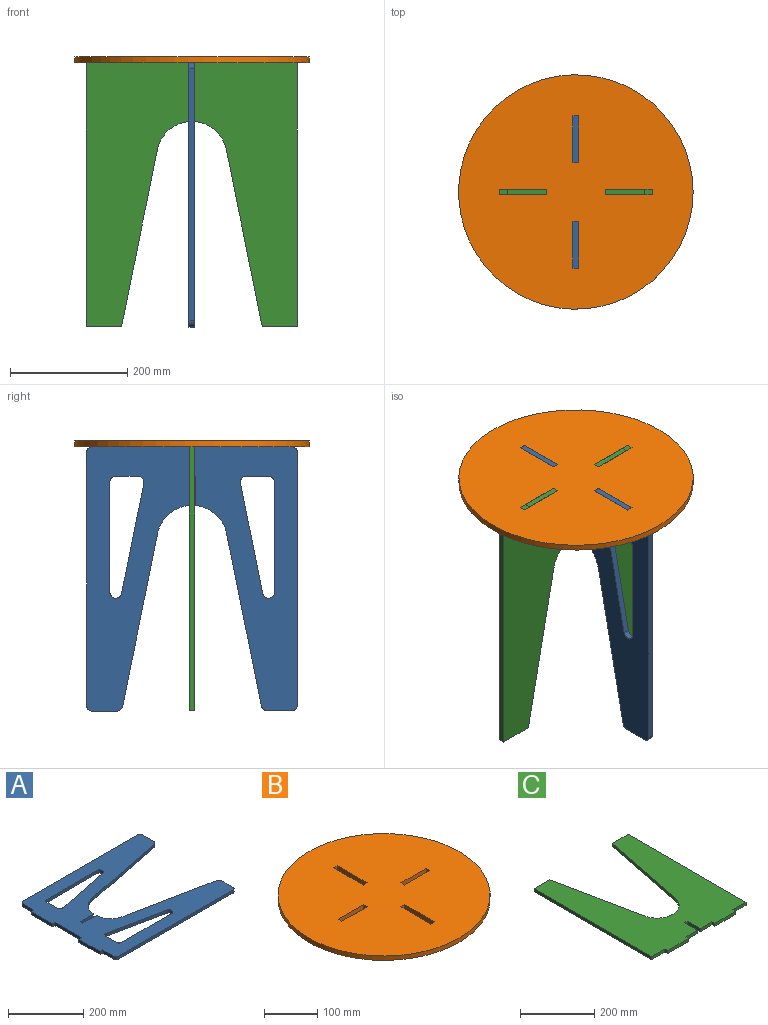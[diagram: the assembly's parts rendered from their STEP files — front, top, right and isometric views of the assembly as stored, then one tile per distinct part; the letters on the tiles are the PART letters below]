
ASSEMBLY  parts=3 mates=2
PART A: 40 faces, bbox 460.6x360x10 mm
  f0: cylinder r=10mm len=10mm, axis (0,0,-1), area 157.1mm2, adj f1,f37,f38,f39
  f1: plane 41.82x10mm, normal (1,0,0), area 418.2mm2, adj f0,f2,f38,f39
  f2: cylinder r=10mm len=10mm, axis (0,0,-1), area 137.2mm2, adj f1,f3,f38,f39
  f3: plane 294.28x59.41mm, normal (0.2,0.98,0), area 3002.1mm2, adj f2,f4,f38,f39
  f4: cylinder r=60mm len=53.81mm, axis (0,0,-1), area 772.9mm2, adj f3,f5,f38,f39
  f5: plane 49.99x10mm, normal (0,1,0), area 499.9mm2, adj f4,f6,f38,f39
  f6: plane 10x10mm, normal (1,0,0), area 100mm2, adj f5,f7,f38,f39
  f7: plane 50x10mm, normal (0,-1,0), area 500mm2, adj f6,f8,f38,f39
  f8: cylinder r=60mm len=53.81mm, axis (0,0,-1), area 772.6mm2, adj f7,f9,f38,f39
  f9: plane 294.95x59.73mm, normal (0.2,-0.98,0), area 3009.3mm2, adj f8,f10,f38,f39
  f10: cylinder r=10mm len=10mm, axis (0,0,-1), area 137.1mm2, adj f9,f11,f38,f39
  f11: plane 41.82x10mm, normal (1,0,0), area 418.2mm2, adj f10,f12,f38,f39
  f12: cylinder r=10mm len=10mm, axis (0,0,-1), area 157.1mm2, adj f11,f13,f38,f39
  f13: plane 430.63x10mm, normal (0,1,0), area 4306.3mm2, adj f12,f14,f38,f39
  f14: cylinder r=10mm len=10mm, axis (0,0,-1), area 157.1mm2, adj f13,f15,f38,f39
  f15: plane 40x10mm, normal (-1,0,0), area 400mm2, adj f14,f16,f38,f39
  f16: plane 10x10mm, normal (0,1,0), area 100mm2, adj f15,f17,f38,f39
  f17: plane 80x10mm, normal (-1,0,0), area 800mm2, adj f16,f18,f38,f39
  f18: plane 10x10mm, normal (0,-1,0), area 100mm2, adj f17,f19,f38,f39
  f19: plane 100x10mm, normal (-1,0,0), area 1000mm2, adj f18,f20,f38,f39
  f20: plane 10x10mm, normal (0,1,0), area 100mm2, adj f19,f21,f38,f39
  f21: plane 80x10mm, normal (-1,0,0), area 800mm2, adj f20,f22,f38,f39
  f22: plane 10x10mm, normal (0,-1,0), area 100mm2, adj f21,f23,f38,f39
  f23: plane 40x10mm, normal (-1,0,0), area 400mm2, adj f22,f24,f38,f39
  f24: cylinder r=10mm len=10mm, axis (0,0,-1), area 157.1mm2, adj f23,f37,f38,f39
  f25: cylinder r=10mm len=11.98mm, axis (0,0,-1), area 177.1mm2, adj f26,f35,f38,f39
  f26: plane 38.09x10mm, normal (1,0,0), area 380.9mm2, adj f25,f27,f38,f39
  f27: cylinder r=10mm len=10mm, axis (0,0,-1), area 157.1mm2, adj f26,f28,f38,f39
  f28: plane 188.09x10mm, normal (0,-1,0), area 1880.9mm2, adj f27,f29,f38,f39
  f29: cylinder r=10mm len=19.8mm, axis (0,0,-1), area 294.2mm2, adj f28,f35,f38,f39
  f30: plane 188.09x10mm, normal (0,1,0), area 1880.9mm2, adj f31,f36,f38,f39
  f31: cylinder r=10mm len=10mm, axis (0,0,-1), area 157.1mm2, adj f30,f32,f38,f39
  f32: plane 38.09x10mm, normal (1,0,0), area 380.9mm2, adj f31,f33,f38,f39
  f33: cylinder r=10mm len=11.98mm, axis (0,0,-1), area 177.1mm2, adj f32,f34,f38,f39
  f34: plane 188.09x38.09mm, normal (-0.2,-0.98,0), area 1919.1mm2, adj f33,f36,f38,f39
  f35: plane 188.09x38.09mm, normal (-0.2,0.98,0), area 1919.1mm2, adj f25,f29,f38,f39
  f36: cylinder r=10mm len=19.8mm, axis (0,0,-1), area 294.2mm2, adj f30,f34,f38,f39
  f37: plane 430x10mm, normal (0,-1,0), area 4300mm2, adj f0,f24,f38,f39
  f38: plane 460.63x360mm, normal (0,0,1), area 88597.3mm2, adj f0,f1,f2,f3,f4,f5,f6,f7
  f39: plane 460.63x360mm, normal (0,0,-1), area 88597.3mm2, adj f0,f1,f2,f3,f4,f5,f6,f7
PART B: 19 faces, bbox 400x400x10 mm
  f0: plane 10x10mm, normal (-1,0,0), area 100mm2, adj f1,f12,f17,f18
  f1: plane 67.44x10mm, normal (0,1,0), area 674.4mm2, adj f0,f2,f17,f18
  f2: plane 10x10mm, normal (1,0,0), area 100mm2, adj f1,f12,f17,f18
  f3: plane 10x10mm, normal (0,1,0), area 100mm2, adj f4,f13,f17,f18
  f4: plane 80x10mm, normal (1,0,0), area 800mm2, adj f3,f5,f17,f18
  f5: plane 10x10mm, normal (0,-1,0), area 100mm2, adj f4,f13,f17,f18
  f6: plane 10x10mm, normal (0,1,0), area 100mm2, adj f7,f14,f17,f18
  f7: plane 80x10mm, normal (1,0,0), area 800mm2, adj f6,f8,f17,f18
  f8: plane 10x10mm, normal (0,-1,0), area 100mm2, adj f7,f14,f17,f18
  f9: plane 67.44x10mm, normal (0,1,0), area 674.4mm2, adj f10,f15,f17,f18
  f10: plane 10x10mm, normal (1,0,0), area 100mm2, adj f9,f11,f17,f18
  f11: plane 67.44x10mm, normal (0,-1,0), area 674.4mm2, adj f10,f15,f17,f18
  f12: plane 67.44x10mm, normal (0,-1,0), area 674.4mm2, adj f0,f2,f17,f18
  f13: plane 80x10mm, normal (-1,0,0), area 800mm2, adj f3,f5,f17,f18
  f14: plane 80x10mm, normal (-1,0,0), area 800mm2, adj f6,f8,f17,f18
  f15: plane 10x10mm, normal (-1,0,0), area 100mm2, adj f9,f11,f17,f18
  f16: cylinder r=200mm len=400mm, axis (0,0,-1), area 12566.4mm2, adj f17,f18
  f17: plane 400x400mm, normal (0,0,1), area 122714.9mm2, adj f0,f1,f2,f3,f4,f5,f6,f7
  f18: plane 400x400mm, normal (0,0,-1), area 122714.9mm2, adj f0,f1,f2,f3,f4,f5,f6,f7
PART C: 22 faces, bbox 360x460x10 mm
  f0: plane 10x10mm, normal (1,0,0), area 100mm2, adj f1,f19,f20,f21
  f1: plane 50x10mm, normal (0,-1,0), area 500mm2, adj f0,f2,f20,f21
  f2: plane 450x10mm, normal (1,0,0), area 4500mm2, adj f1,f3,f20,f21
  f3: plane 60x10mm, normal (0,1,0), area 600mm2, adj f2,f4,f20,f21
  f4: plane 301.92x61.2mm, normal (-0.98,0.2,0), area 3080.6mm2, adj f3,f5,f20,f21
  f5: cylinder r=60mm len=117.61mm, axis (0,0,-1), area 1645mm2, adj f4,f6,f20,f21
  f6: plane 301.92x61.2mm, normal (0.98,0.2,0), area 3080.6mm2, adj f5,f7,f20,f21
  f7: plane 60x10mm, normal (0,1,0), area 600mm2, adj f6,f8,f20,f21
  f8: plane 450x10mm, normal (-1,0,0), area 4500mm2, adj f7,f9,f20,f21
  f9: plane 50x10mm, normal (0,-1,0), area 500mm2, adj f8,f10,f20,f21
  f10: plane 10x10mm, normal (-1,0,0), area 100mm2, adj f9,f11,f20,f21
  f11: plane 80x10mm, normal (0,-1,0), area 800mm2, adj f10,f12,f20,f21
  f12: plane 10x10mm, normal (1,0,0), area 100mm2, adj f11,f13,f20,f21
  f13: plane 45x10mm, normal (0,-1,0), area 450mm2, adj f12,f14,f20,f21
  f14: plane 50x10mm, normal (1,0,0), area 500mm2, adj f13,f15,f20,f21
  f15: plane 10x10mm, normal (0,-1,0), area 100mm2, adj f14,f16,f20,f21
  f16: plane 50x10mm, normal (-1,0,0), area 500mm2, adj f15,f17,f20,f21
  f17: plane 45x10mm, normal (0,-1,0), area 450mm2, adj f16,f18,f20,f21
  f18: plane 10x10mm, normal (-1,0,0), area 100mm2, adj f17,f19,f20,f21
  f19: plane 80x10mm, normal (0,-1,0), area 800mm2, adj f0,f18,f20,f21
  f20: plane 460x360mm, normal (0,0,1), area 104881.6mm2, adj f0,f1,f2,f3,f4,f5,f6,f7
  f21: plane 460x360mm, normal (0,0,-1), area 104881.6mm2, adj f0,f1,f2,f3,f4,f5,f6,f7
PLACE A rot(axis=(0,1,0),90deg) t=(-156.08,-94.77,287.92)mm
PLACE B t=(-151.08,-94.47,-15.87)mm fixed
PLACE C rot(axis=(-1,0,0),90deg) t=(-151.08,-99.47,232.78)mm
MATE planar C.f12 <-> B.f0  axis (1,0,0) through (-201.08,-94.47,-10.87)mm
MATE planar A.f18 <-> B.f6  axis (0,-1,0) through (-151.08,-44.47,-11.08)mm
